AUTODESK INVENTOR PART (.ipt)
format: ipt  version: 2019 (Build 230136000, 136)  size: 12,902,400 bytes
history: native  units: mm
features: extrude x8, other x6, sketch x2, projected_geometry x1
ambient origin geometry x8: Origin, YZ Plane, XZ Plane, XY Plane, X Axis, Y Axis, Z Axis, Center Point
bodies: Body1 (feature_tree), Body2 (feature_tree), Body3 (feature_tree)
feature tree (17):
  other  "Твердое тело1"
  sketch  "Эскиз1"
  extrude  "Стены кап"  Depth=5600.0mm
  extrude  "Перегородки"  Depth=3000.0mm
  extrude  "Короб"  Depth=8400.0mm
  other  "РабПлоскость2"
  extrude  "Окна"  Depth=3000.0mm
  extrude  "Двери"  Depth=5600.0mm
  extrude  "Ворота"  Depth=1200.0mm
  extrude  "Двери межкомнатные"  Depth=3000.0mm
  extrude  "Выдавливание8"  Depth=2400.0mm
  other  "Картинка1"
  other  "Твердое тело2"
  other  "Твердое тело3"
  other  "РабПлоскость1"
  sketch  "Эскиз2"
  projected_geometry  "Спроецированная петля1"
